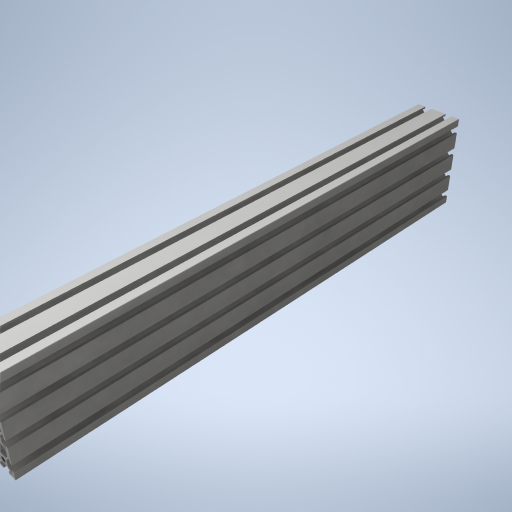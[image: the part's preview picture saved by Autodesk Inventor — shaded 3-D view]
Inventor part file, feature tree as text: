
AUTODESK INVENTOR PART (.ipt)
format: ipt  version: 2024 (Build 280153000, 153)  size: 689,152 bytes
history: native  units: mm
features: thread x16, sketch x2, extrude x1, hole x1, pattern_linear x1
ambient origin geometry x8: Origin, YZ Plane, XZ Plane, XY Plane, X Axis, Y Axis, Z Axis, Center Point
bodies: Solid1 (feature_tree)
feature tree (21):
  extrude  "Extrusion1"  Depth=20.0mm
  hole  "Hole1"  [1 undecoded]
  pattern_linear  "Rectangular Pattern1"  Spacing1=10.0mm  [1 undecoded]
  thread  "Thread2"  [1 undecoded]
  thread  "Thread3"  [1 undecoded]
  thread  "Thread4"  [1 undecoded]
  thread  "Thread5"  [1 undecoded]
  thread  "Thread6"  [1 undecoded]
  thread  "Thread7"  [1 undecoded]
  thread  "Thread8"  [1 undecoded]
  thread  "Thread9"  [1 undecoded]
  thread  "Thread10"  [1 undecoded]
  thread  "Thread11"  [1 undecoded]
  thread  "Thread12"  [1 undecoded]
  thread  "Thread13"  [1 undecoded]
  thread  "Thread14"  [1 undecoded]
  thread  "Thread15"  [1 undecoded]
  thread  "Thread16"  [1 undecoded]
  thread  "Thread17"  [1 undecoded]
  sketch  "Sketch_118"  dims[d2=4.2mm d3=6.0mm d4=4.0mm d5=2.0mm d6=90.0deg d7=425.0mm d8=0.0mm d9=20.0mm d11=20.0mm d12=20.0mm d14=60.0mm d17=10.0mm d18=0.0mm d19=10.0mm d20=0.0mm d21=10.0mm d22=0.0mm d23=10.0mm d24=0.0mm d25=10.0mm d26=0.0mm d27=10.0mm d28=0.0mm d29=10.0mm d30=0.0mm d31=10.0mm d32=0.0mm d33=10.0mm d34=0.0mm d35=10.0mm d36=0.0mm d37=10.0mm d38=0.0mm d39=10.0mm d40=0.0mm d41=10.0mm d42=0.0mm d43=10.0mm d44=0.0mm d45=10.0mm d46=0.0mm d47=10.0mm d48=0.0mm]
  sketch  "Sketch2"  dims[d0=425.0mm d1=0.0mm]
note: 18 required parameter values undecoded (feature->parameter linkage not recoverable at this tier; creation-order binding heuristic only, values carry confidence <= 0.55)
